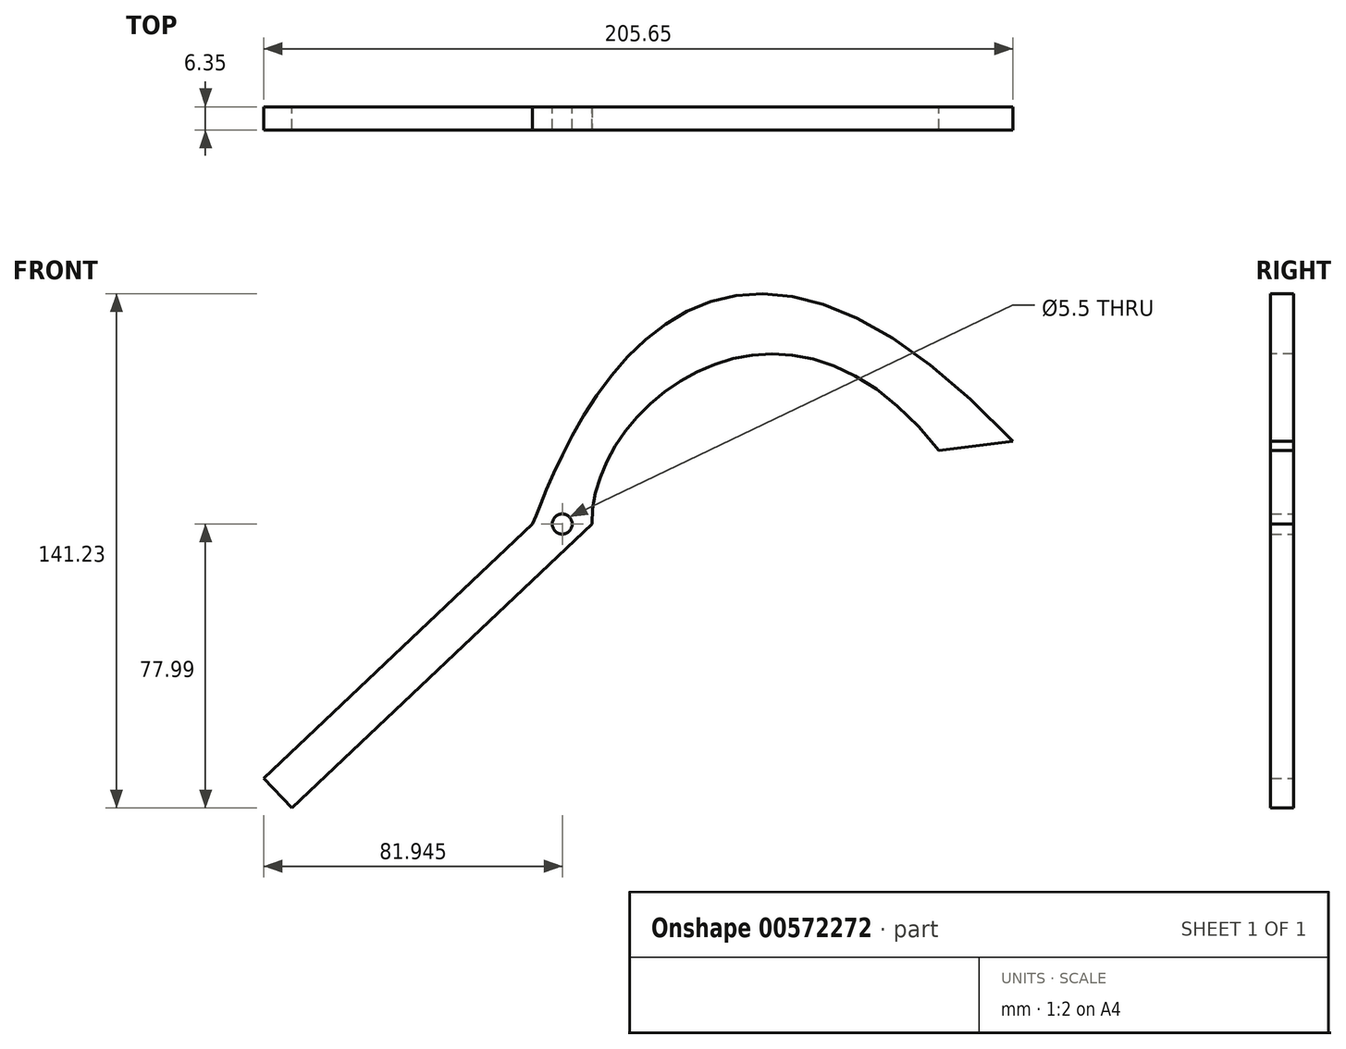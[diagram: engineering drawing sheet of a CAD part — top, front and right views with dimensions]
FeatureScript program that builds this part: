
annotation { "Feature Type Name" : "Feature", "Feature Type Description" : "" }
export const myFeature = defineFeature(function(context is Context, id is Id, definition is map)
    precondition{}
    {
        {
            var Q0;
            Q0=qCreatedBy(makeId("Front.planeOp"),FACE);
            var sketch = newSketch(context, id + "F0", { "sketchPlane" : qUnion([Q0])});
            skFitSpline(sketch, "E0", {"points": [v(-40.1, 0) * mm, v(91.76, 22.74) * mm], "startDerivative": vector(17.78, 40.68) * mm, "endDerivative": vector(275.29, -291.35) * mm});
            skFitSpline(sketch, "E1", {"points": [v(71.54, 20.14) * mm, v(-23.79, 0) * mm], "startDerivative": vector(-129.1, 166.42) * mm, "endDerivative": vector(2.7, -96.2) * mm});
            skLineSegment(sketch, "E2", {"start": v(-40.1, 0) * mm, "end": v(-23.79, 0) * mm});
            skCircle(sketch, "E3", {"center": v(-31.94, 0) * mm, "radius": 2.75 * mm});
            skLineSegment(sketch, "E4", {"start": v(71.54, 20.14) * mm, "end": v(91.76, 22.74) * mm});
            skLineSegment(sketch, "E5", {"start": v(-40.1, 0) * mm, "end": v(-113.89, -69.84) * mm});
            skLineSegment(sketch, "E6", {"start": v(-113.89, -69.84) * mm, "end": v(-106.18, -77.99) * mm});
            skLineSegment(sketch, "E7", {"start": v(-106.18, -77.99) * mm, "end": v(-23.79, 0) * mm});
            skLineSegment(sketch, "E8", {"start": v(-23.79, 0) * mm, "end": v(-40.1, 0) * mm});
            skSolve(sketch);
        }
        {
            var Q0;
            {var subQ5=sQuery(id+"F0.wireOp",EDGE,"E0");Q0=makeQuery(id+"F0.imprint","IMPRINT",FACE,{"disambiguationData":[TD([[makeQuery(id+"F0.imprint","IMPRINT",EDGE,{"derivedFrom":subQ5}),-1.0]])]});}
            var Q1;
            {var subQ0=sQuery(id+"F0.wireOp",EDGE,"E5");Q1=makeQuery(id+"F0.imprint","IMPRINT",FACE,{"disambiguationData":[TD([[makeQuery(id+"F0.imprint","IMPRINT",EDGE,{"derivedFrom":subQ0}),1.0]])]});}
            extrude(context, id + "F1", {"entities" : qUnion([Q0, Q1]), "depth" : 6.35 * mm, "offsetDistance" : 25.4 * mm});
        }
    });
